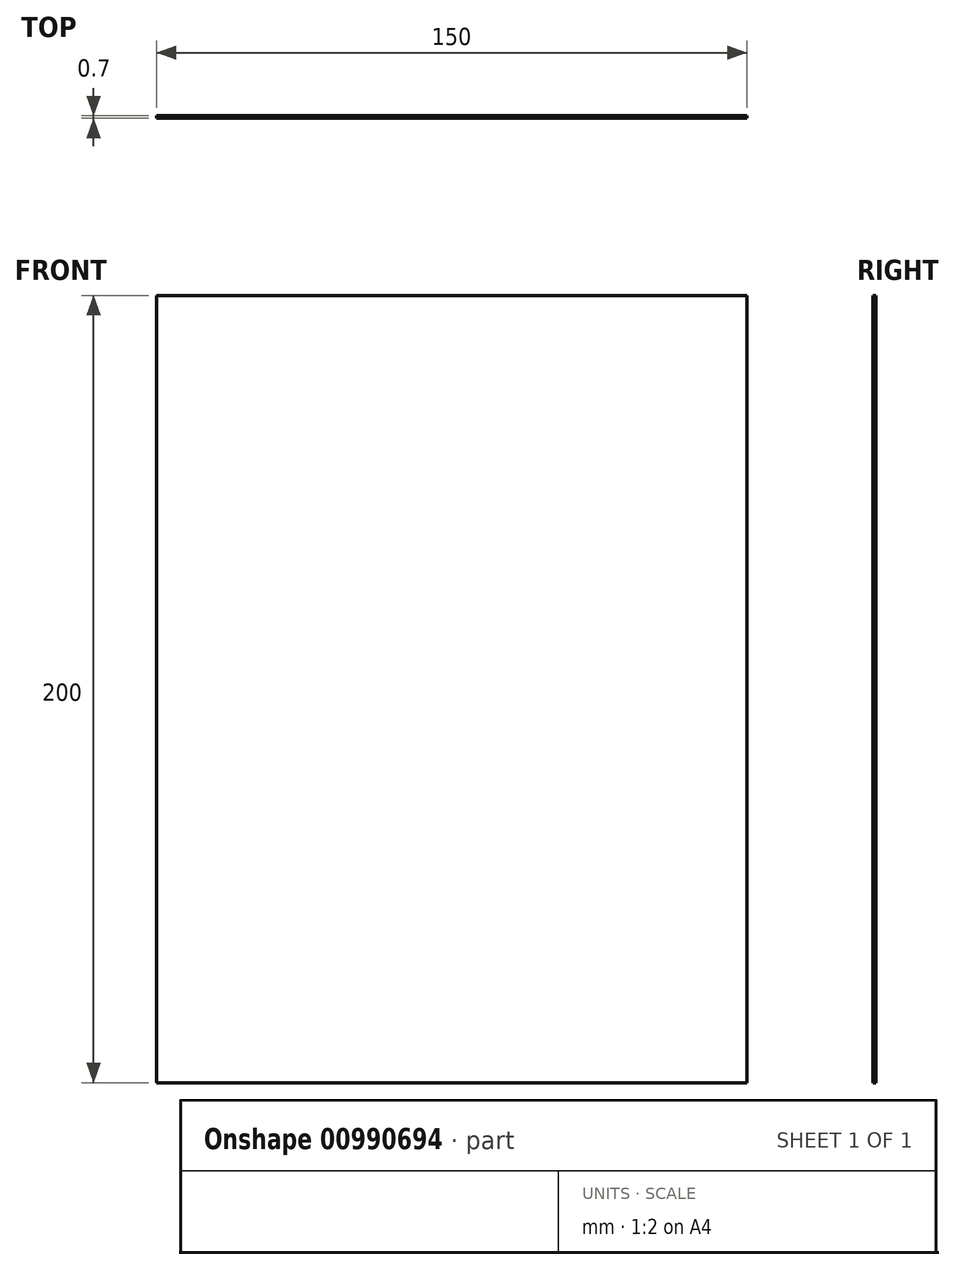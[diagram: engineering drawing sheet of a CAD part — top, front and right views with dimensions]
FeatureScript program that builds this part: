
annotation { "Feature Type Name" : "Feature", "Feature Type Description" : "" }
export const myFeature = defineFeature(function(context is Context, id is Id, definition is map)
    precondition{}
    {
        {
            assignVariable(context, id + "F0", {"variableType" : VariableType.LENGTH, "name" : "DiffuserThickness", "lengthValue" : 0.7 * mm});
        }
        {
            var Q0;
            Q0=qCreatedBy(makeId("Front.planeOp"),FACE);
            var sketch = newSketch(context, id + "F1", { "sketchPlane" : qUnion([Q0])});
            skLineSegment(sketch, "E0.bottom", {"start": v(75, -100) * mm, "end": v(-75, -100) * mm});
            skLineSegment(sketch, "E0.top", {"start": v(75, 100) * mm, "end": v(-75, 100) * mm});
            skLineSegment(sketch, "E0.left", {"start": v(75, -100) * mm, "end": v(75, 100) * mm});
            skLineSegment(sketch, "E0.right", {"start": v(-75, -100) * mm, "end": v(-75, 100) * mm});
            skPoint(sketch, "E0.middle", {"position": v(0, 0) * mm});
            skSolve(sketch);
        }
        {
            var Q0;
            Q0 = qSketchRegion(id + "F1", true);
            extrude(context, id + "F2", {"entities" : qUnion([Q0]), "depth" : getVariable(context, 'DiffuserThickness'), "offsetDistance" : 25 * mm});
        }
    });
